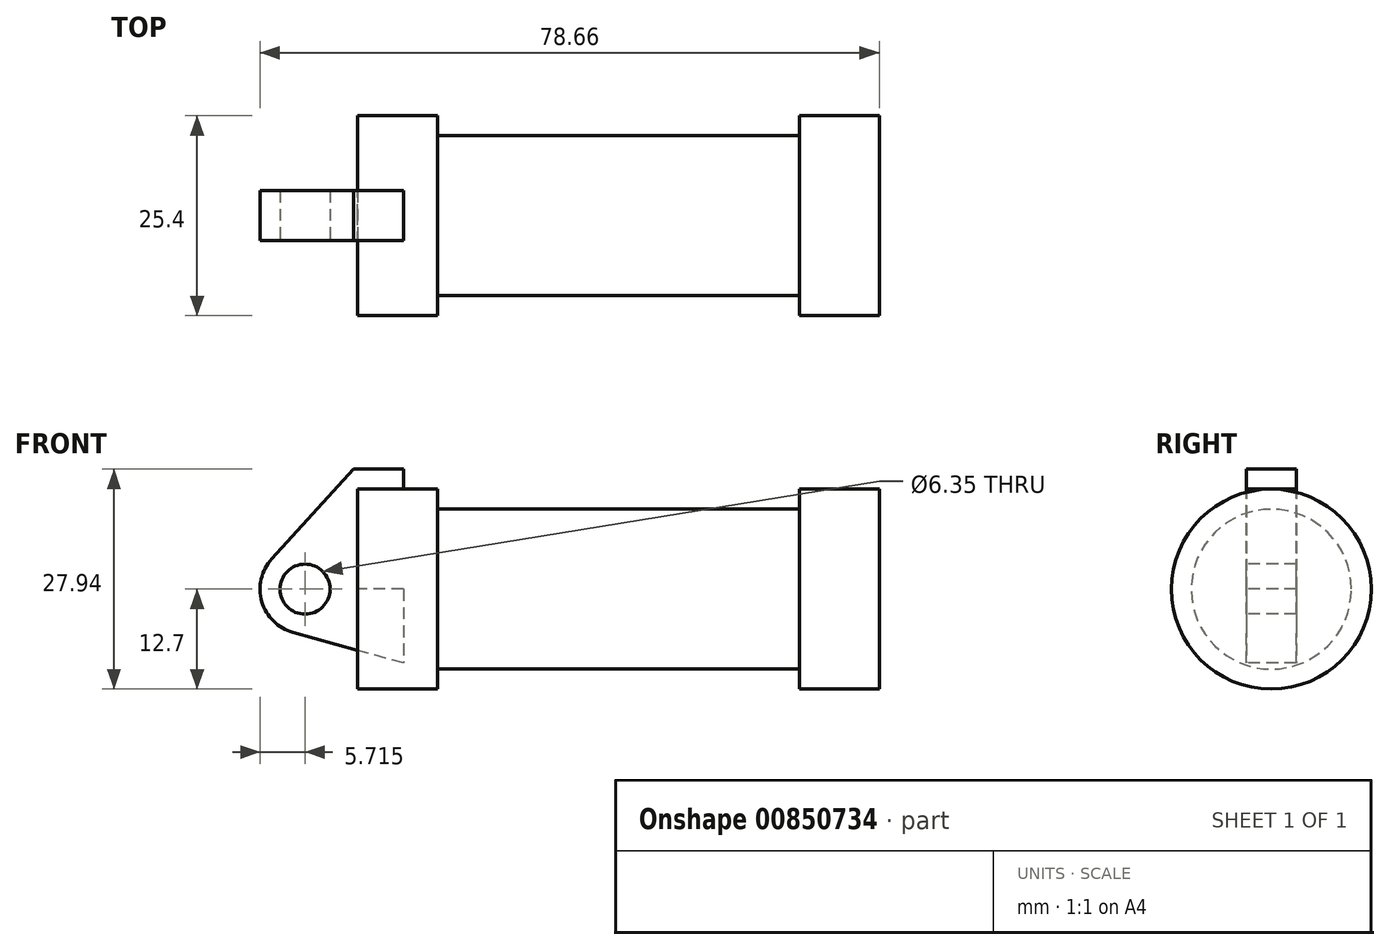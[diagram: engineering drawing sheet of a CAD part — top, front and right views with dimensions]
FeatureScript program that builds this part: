
annotation { "Feature Type Name" : "Feature", "Feature Type Description" : "" }
export const myFeature = defineFeature(function(context is Context, id is Id, definition is map)
    precondition{}
    {
        {
            var Q0;
            Q0=qCreatedBy(makeId("Front.planeOp"),FACE);
            var sketch = newSketch(context, id + "F0", { "sketchPlane" : qUnion([Q0])});
            skLineSegment(sketch, "E0", {"start": v(0, 0) * mm, "end": v(0, 12.7) * mm});
            skLineSegment(sketch, "E1", {"start": v(0, 12.7) * mm, "end": v(10.16, 12.7) * mm});
            skLineSegment(sketch, "E2", {"start": v(10.16, 12.7) * mm, "end": v(10.16, 10.16) * mm});
            skLineSegment(sketch, "E3", {"start": v(10.16, 10.16) * mm, "end": v(56.13, 10.16) * mm});
            skLineSegment(sketch, "E4", {"start": v(56.13, 10.16) * mm, "end": v(56.13, 12.7) * mm});
            skLineSegment(sketch, "E5", {"start": v(56.13, 12.7) * mm, "end": v(66.3, 12.7) * mm});
            skLineSegment(sketch, "E6", {"start": v(66.3, 12.7) * mm, "end": v(66.3, 0) * mm});
            skLineSegment(sketch, "E7", {"start": v(66.3, 0) * mm, "end": v(0, 0) * mm});
            skLineSegment(sketch, "E8", {"start": v(5.84, 15.24) * mm, "end": v(-0.5, 15.24) * mm});
            skLineSegment(sketch, "E9", {"start": v(-0.5, 15.24) * mm, "end": v(-10.88, 3.85) * mm});
            skLineSegment(sketch, "E10", {"start": v(0, 0) * mm, "end": v(-6.65, 0) * mm});
            skCircle(sketch, "E11", {"center": v(-6.65, 0) * mm, "radius": 5.72 * mm});
            skCircle(sketch, "E12", {"center": v(-6.65, 0) * mm, "radius": 3.18 * mm});
            skLineSegment(sketch, "E13", {"start": v(5.84, 15.24) * mm, "end": v(5.84, -9.4) * mm});
            skLineSegment(sketch, "E14", {"start": v(5.84, -9.4) * mm, "end": v(-8.18, -5.5) * mm});
            skSolve(sketch);
        }
        {
            var Q0;
            {var subQ0=sQuery(id+"F0.wireOp",EDGE,"E0");Q0=makeQuery(id+"F0.imprint","IMPRINT",FACE,{"disambiguationData":[TD([[makeQuery(id+"F0.imprint","IMPRINT",EDGE,{"derivedFrom":subQ0}),-1.0]])]});}
            var Q1;
            {var subQ0=sQuery(id+"F0.wireOp",EDGE,"E2");Q1=makeQuery(id+"F0.imprint","IMPRINT",FACE,{"disambiguationData":[TD([[makeQuery(id+"F0.imprint","IMPRINT",EDGE,{"derivedFrom":subQ0}),-1.0]])]});}
            var Q2;
            Q2=sQuery(id+"F0.wireOp",EDGE,"E7");
            revolve(context, id + "F1", {"surfaceOperationType" : NewSurfaceOperationType.NEW, "entities" : qUnion([Q0, Q1]), "axis" : qUnion([Q2]), "revolveType" : RevolveType.FULL});
        }
        {
            var Q0;
            {var subQ1=sQuery(id+"F0.wireOp",EDGE,"E0");Q0=makeQuery(id+"F0.imprint","IMPRINT",FACE,{"disambiguationData":[TD([[makeQuery(id+"F0.imprint","IMPRINT",EDGE,{"derivedFrom":subQ1}),1.0]])]});}
            var Q1;
            {var subQ5=sQuery(id+"F0.wireOp",EDGE,"E12");Q1=makeQuery(id+"F0.imprint","IMPRINT",FACE,{"disambiguationData":[TD([[makeQuery(id+"F0.imprint","IMPRINT",EDGE,{"derivedFrom":subQ5}),-1.0]])]});}
            var Q2;
            {var subQ0=sQuery(id+"F0.wireOp",EDGE,"E14");Q2=makeQuery(id+"F0.imprint","IMPRINT",FACE,{"disambiguationData":[TD([[makeQuery(id+"F0.imprint","IMPRINT",EDGE,{"derivedFrom":subQ0}),-1.0]])]});}
            extrude(context, id + "F2", {"entities" : qUnion([Q0, Q1, Q2]), "depth" : 6.35 * mm, "offsetDistance" : 25.4 * mm});
        }
        {
            var Q0;
            Q0=makeQuery(id+"F2.opExtrude","SWEPT_BODY",BODY,{"disambiguationData":[OSD([sQuery(id+"F0.wireOp",EDGE,"E0"),sQuery(id+"F0.wireOp",EDGE,"E1"),sQuery(id+"F0.wireOp",EDGE,"E7"),sQuery(id+"F0.wireOp",EDGE,"E8"),sQuery(id+"F0.wireOp",EDGE,"E9"),sQuery(id+"F0.wireOp",EDGE,"E11"),sQuery(id+"F0.wireOp",EDGE,"E12"),sQuery(id+"F0.wireOp",EDGE,"E13"),sQuery(id+"F0.wireOp",EDGE,"E14")])]});
            deleteBodies(context, id + "F3", {"entities" : qUnion([Q0])});
        }
        {
            var Q0;
            {var subQ5=sQuery(id+"F0.wireOp",EDGE,"E12");Q0=makeQuery(id+"F0.imprint","IMPRINT",FACE,{"disambiguationData":[TD([[makeQuery(id+"F0.imprint","IMPRINT",EDGE,{"derivedFrom":subQ5}),-1.0]])]});}
            var Q1;
            {var subQ1=sQuery(id+"F0.wireOp",EDGE,"E0");Q1=makeQuery(id+"F0.imprint","IMPRINT",FACE,{"disambiguationData":[TD([[makeQuery(id+"F0.imprint","IMPRINT",EDGE,{"derivedFrom":subQ1}),1.0]])]});}
            var Q2;
            {var subQ0=sQuery(id+"F0.wireOp",EDGE,"E14");Q2=makeQuery(id+"F0.imprint","IMPRINT",FACE,{"disambiguationData":[TD([[makeQuery(id+"F0.imprint","IMPRINT",EDGE,{"derivedFrom":subQ0}),-1.0]])]});}
            extrude(context, id + "F4", {"entities" : qUnion([Q0, Q1, Q2]), "endBound" : BoundingType.SYMMETRIC, "oppositeDirection" : true, "depth" : 6.35 * mm, "offsetDistance" : 25.4 * mm});
        }
        {
            var Q0;
            Q0=makeQuery(id+"F1.opRevolve","SWEPT_BODY",BODY,{"disambiguationData":[OSD([sQuery(id+"F0.wireOp",EDGE,"E0"),sQuery(id+"F0.wireOp",EDGE,"E1"),sQuery(id+"F0.wireOp",EDGE,"E2"),sQuery(id+"F0.wireOp",EDGE,"E3"),sQuery(id+"F0.wireOp",EDGE,"E4"),sQuery(id+"F0.wireOp",EDGE,"E5"),sQuery(id+"F0.wireOp",EDGE,"E6"),sQuery(id+"F0.wireOp",EDGE,"E7")])]});
            var Q1;
            Q1=makeQuery(id+"F4.opExtrude","SWEPT_BODY",BODY,{"disambiguationData":[OSD([sQuery(id+"F0.wireOp",EDGE,"E0"),sQuery(id+"F0.wireOp",EDGE,"E1"),sQuery(id+"F0.wireOp",EDGE,"E7"),sQuery(id+"F0.wireOp",EDGE,"E8"),sQuery(id+"F0.wireOp",EDGE,"E9"),sQuery(id+"F0.wireOp",EDGE,"E11"),sQuery(id+"F0.wireOp",EDGE,"E12"),sQuery(id+"F0.wireOp",EDGE,"E13"),sQuery(id+"F0.wireOp",EDGE,"E14")])]});
            var Q2;
            Q2=sQuery(id+"F0.wireOp",EDGE,"E7");
            circularPattern(context, id + "F5", {"entities" : qUnion([Q0, Q1]), "axis" : qUnion([Q2]), "angle" : 360 * degree, "instanceCount" : 4, "isCentered" : true});
        }
        {
            var Q0;
            Q0=makeQuery(id+"F5.opPattern","COPY",BODY,{"derivedFrom":makeQuery(id+"F1.opRevolve","SWEPT_BODY",BODY,{"disambiguationData":[OSD([sQuery(id+"F0.wireOp",EDGE,"E0"),sQuery(id+"F0.wireOp",EDGE,"E1"),sQuery(id+"F0.wireOp",EDGE,"E2"),sQuery(id+"F0.wireOp",EDGE,"E3"),sQuery(id+"F0.wireOp",EDGE,"E4"),sQuery(id+"F0.wireOp",EDGE,"E5"),sQuery(id+"F0.wireOp",EDGE,"E6"),sQuery(id+"F0.wireOp",EDGE,"E7")])]}),"instanceName":"1"});
            deleteBodies(context, id + "F6", {"entities" : qUnion([Q0])});
        }
        {
            var Q0;
            Q0=makeQuery(id+"F5.opPattern","COPY",BODY,{"derivedFrom":makeQuery(id+"F4.opExtrude","SWEPT_BODY",BODY,{"disambiguationData":[OSD([sQuery(id+"F0.wireOp",EDGE,"E0"),sQuery(id+"F0.wireOp",EDGE,"E1"),sQuery(id+"F0.wireOp",EDGE,"E7"),sQuery(id+"F0.wireOp",EDGE,"E8"),sQuery(id+"F0.wireOp",EDGE,"E9"),sQuery(id+"F0.wireOp",EDGE,"E11"),sQuery(id+"F0.wireOp",EDGE,"E12"),sQuery(id+"F0.wireOp",EDGE,"E13"),sQuery(id+"F0.wireOp",EDGE,"E14")])]}),"instanceName":"-1"});
            deleteBodies(context, id + "F7", {"entities" : qUnion([Q0])});
        }
        {
            var Q0;
            Q0=makeQuery(id+"F5.opPattern","COPY",BODY,{"derivedFrom":makeQuery(id+"F1.opRevolve","SWEPT_BODY",BODY,{"disambiguationData":[OSD([sQuery(id+"F0.wireOp",EDGE,"E0"),sQuery(id+"F0.wireOp",EDGE,"E1"),sQuery(id+"F0.wireOp",EDGE,"E2"),sQuery(id+"F0.wireOp",EDGE,"E3"),sQuery(id+"F0.wireOp",EDGE,"E4"),sQuery(id+"F0.wireOp",EDGE,"E5"),sQuery(id+"F0.wireOp",EDGE,"E6"),sQuery(id+"F0.wireOp",EDGE,"E7")])]}),"instanceName":"-1"});
            var Q1;
            Q1=makeQuery(id+"F5.opPattern","COPY",BODY,{"derivedFrom":makeQuery(id+"F4.opExtrude","SWEPT_BODY",BODY,{"disambiguationData":[OSD([sQuery(id+"F0.wireOp",EDGE,"E0"),sQuery(id+"F0.wireOp",EDGE,"E1"),sQuery(id+"F0.wireOp",EDGE,"E7"),sQuery(id+"F0.wireOp",EDGE,"E8"),sQuery(id+"F0.wireOp",EDGE,"E9"),sQuery(id+"F0.wireOp",EDGE,"E11"),sQuery(id+"F0.wireOp",EDGE,"E12"),sQuery(id+"F0.wireOp",EDGE,"E13"),sQuery(id+"F0.wireOp",EDGE,"E14")])]}),"instanceName":"-2"});
            deleteBodies(context, id + "F8", {"entities" : qUnion([Q0, Q1])});
        }
        {
            var Q0;
            Q0=makeQuery(id+"F5.opPattern","COPY",BODY,{"derivedFrom":makeQuery(id+"F1.opRevolve","SWEPT_BODY",BODY,{"disambiguationData":[OSD([sQuery(id+"F0.wireOp",EDGE,"E0"),sQuery(id+"F0.wireOp",EDGE,"E1"),sQuery(id+"F0.wireOp",EDGE,"E2"),sQuery(id+"F0.wireOp",EDGE,"E3"),sQuery(id+"F0.wireOp",EDGE,"E4"),sQuery(id+"F0.wireOp",EDGE,"E5"),sQuery(id+"F0.wireOp",EDGE,"E6"),sQuery(id+"F0.wireOp",EDGE,"E7")])]}),"instanceName":"3"});
            var Q1;
            Q1=makeQuery(id+"F5.opPattern","COPY",BODY,{"derivedFrom":makeQuery(id+"F4.opExtrude","SWEPT_BODY",BODY,{"disambiguationData":[OSD([sQuery(id+"F0.wireOp",EDGE,"E0"),sQuery(id+"F0.wireOp",EDGE,"E1"),sQuery(id+"F0.wireOp",EDGE,"E7"),sQuery(id+"F0.wireOp",EDGE,"E8"),sQuery(id+"F0.wireOp",EDGE,"E9"),sQuery(id+"F0.wireOp",EDGE,"E11"),sQuery(id+"F0.wireOp",EDGE,"E12"),sQuery(id+"F0.wireOp",EDGE,"E13"),sQuery(id+"F0.wireOp",EDGE,"E14")])]}),"instanceName":"2"});
            var Q2;
            Q2=makeQuery(id+"F5.opPattern","COPY",BODY,{"derivedFrom":makeQuery(id+"F1.opRevolve","SWEPT_BODY",BODY,{"disambiguationData":[OSD([sQuery(id+"F0.wireOp",EDGE,"E0"),sQuery(id+"F0.wireOp",EDGE,"E1"),sQuery(id+"F0.wireOp",EDGE,"E2"),sQuery(id+"F0.wireOp",EDGE,"E3"),sQuery(id+"F0.wireOp",EDGE,"E4"),sQuery(id+"F0.wireOp",EDGE,"E5"),sQuery(id+"F0.wireOp",EDGE,"E6"),sQuery(id+"F0.wireOp",EDGE,"E7")])]}),"instanceName":"2"});
            var Q3;
            Q3=makeQuery(id+"F5.opPattern","COPY",BODY,{"derivedFrom":makeQuery(id+"F4.opExtrude","SWEPT_BODY",BODY,{"disambiguationData":[OSD([sQuery(id+"F0.wireOp",EDGE,"E0"),sQuery(id+"F0.wireOp",EDGE,"E1"),sQuery(id+"F0.wireOp",EDGE,"E7"),sQuery(id+"F0.wireOp",EDGE,"E8"),sQuery(id+"F0.wireOp",EDGE,"E9"),sQuery(id+"F0.wireOp",EDGE,"E11"),sQuery(id+"F0.wireOp",EDGE,"E12"),sQuery(id+"F0.wireOp",EDGE,"E13"),sQuery(id+"F0.wireOp",EDGE,"E14")])]}),"instanceName":"1"});
            var Q4;
            Q4=makeQuery(id+"F5.opPattern","COPY",BODY,{"derivedFrom":makeQuery(id+"F1.opRevolve","SWEPT_BODY",BODY,{"disambiguationData":[OSD([sQuery(id+"F0.wireOp",EDGE,"E0"),sQuery(id+"F0.wireOp",EDGE,"E1"),sQuery(id+"F0.wireOp",EDGE,"E2"),sQuery(id+"F0.wireOp",EDGE,"E3"),sQuery(id+"F0.wireOp",EDGE,"E4"),sQuery(id+"F0.wireOp",EDGE,"E5"),sQuery(id+"F0.wireOp",EDGE,"E6"),sQuery(id+"F0.wireOp",EDGE,"E7")])]}),"instanceName":"-2"});
            var Q5;
            Q5=makeQuery(id+"F5.opPattern","COPY",BODY,{"derivedFrom":makeQuery(id+"F4.opExtrude","SWEPT_BODY",BODY,{"disambiguationData":[OSD([sQuery(id+"F0.wireOp",EDGE,"E0"),sQuery(id+"F0.wireOp",EDGE,"E1"),sQuery(id+"F0.wireOp",EDGE,"E7"),sQuery(id+"F0.wireOp",EDGE,"E8"),sQuery(id+"F0.wireOp",EDGE,"E9"),sQuery(id+"F0.wireOp",EDGE,"E11"),sQuery(id+"F0.wireOp",EDGE,"E12"),sQuery(id+"F0.wireOp",EDGE,"E13"),sQuery(id+"F0.wireOp",EDGE,"E14")])]}),"instanceName":"3"});
            deleteBodies(context, id + "F9", {"entities" : qUnion([Q0, Q1, Q2, Q3, Q4, Q5])});
        }
        {
            var Q0;
            Q0=makeQuery(id+"F5.opPattern","COPY",BODY,{"derivedFrom":makeQuery(id+"F4.opExtrude","SWEPT_BODY",BODY,{"disambiguationData":[OSD([sQuery(id+"F0.wireOp",EDGE,"E0"),sQuery(id+"F0.wireOp",EDGE,"E1"),sQuery(id+"F0.wireOp",EDGE,"E7"),sQuery(id+"F0.wireOp",EDGE,"E8"),sQuery(id+"F0.wireOp",EDGE,"E9"),sQuery(id+"F0.wireOp",EDGE,"E11"),sQuery(id+"F0.wireOp",EDGE,"E12"),sQuery(id+"F0.wireOp",EDGE,"E13"),sQuery(id+"F0.wireOp",EDGE,"E14")])]}),"instanceName":"-3"});
            deleteBodies(context, id + "F10", {"entities" : qUnion([Q0])});
        }
        {
            var Q0;
            Q0=makeQuery(id+"F5.opPattern","COPY",BODY,{"derivedFrom":makeQuery(id+"F1.opRevolve","SWEPT_BODY",BODY,{"disambiguationData":[OSD([sQuery(id+"F0.wireOp",EDGE,"E0"),sQuery(id+"F0.wireOp",EDGE,"E1"),sQuery(id+"F0.wireOp",EDGE,"E2"),sQuery(id+"F0.wireOp",EDGE,"E3"),sQuery(id+"F0.wireOp",EDGE,"E4"),sQuery(id+"F0.wireOp",EDGE,"E5"),sQuery(id+"F0.wireOp",EDGE,"E6"),sQuery(id+"F0.wireOp",EDGE,"E7")])]}),"instanceName":"-3"});
            deleteBodies(context, id + "F11", {"entities" : qUnion([Q0])});
        }
    });
